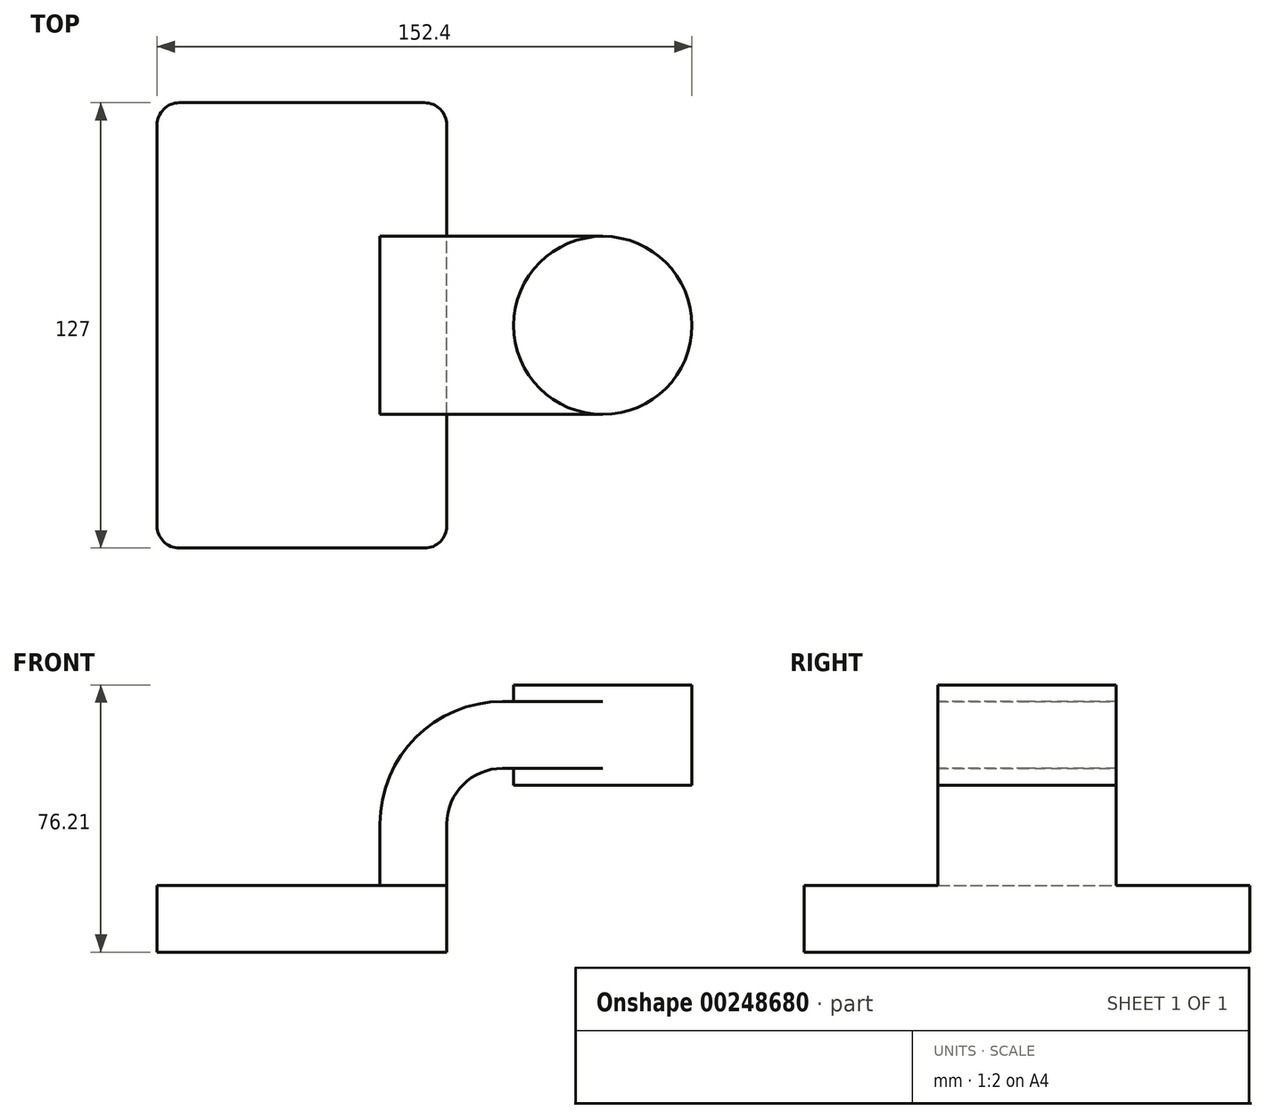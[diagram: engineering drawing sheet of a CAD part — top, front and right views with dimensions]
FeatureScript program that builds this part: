
annotation { "Feature Type Name" : "Feature", "Feature Type Description" : "" }
export const myFeature = defineFeature(function(context is Context, id is Id, definition is map)
    precondition{}
    {
        {
            var Q0;
            Q0=qCreatedBy(makeId("Front.planeOp"),FACE);
            var sketch = newSketch(context, id + "F0", { "sketchPlane" : qUnion([Q0])});
            skLineSegment(sketch, "E0.bottom", {"start": v(-41.28, 9.52) * mm, "end": v(41.27, 9.53) * mm});
            skLineSegment(sketch, "E0.top", {"start": v(-41.28, -9.53) * mm, "end": v(41.28, -9.53) * mm});
            skLineSegment(sketch, "E0.left", {"start": v(-41.28, 9.52) * mm, "end": v(-41.27, -9.53) * mm});
            skLineSegment(sketch, "E0.right", {"start": v(41.28, 9.53) * mm, "end": v(41.28, -9.52) * mm});
            skPoint(sketch, "E0.middle", {"position": v(0, 0) * mm});
            skLineSegment(sketch, "E1.bottom", {"start": v(60.32, 66.68) * mm, "end": v(111.12, 66.68) * mm});
            skLineSegment(sketch, "E1.top", {"start": v(60.33, 38.1) * mm, "end": v(111.12, 38.1) * mm});
            skLineSegment(sketch, "E1.left", {"start": v(60.32, 66.68) * mm, "end": v(60.33, 38.1) * mm});
            skLineSegment(sketch, "E1.right", {"start": v(111.12, 66.68) * mm, "end": v(111.12, 38.1) * mm});
            skPoint(sketch, "E1.middle", {"position": v(85.72, 52.39) * mm});
            skLineSegment(sketch, "E2", {"start": v(41.27, 9.53) * mm, "end": v(41.27, 27) * mm});
            skArc(sketch, "E3", {"start": v(41.27, 27) * mm, "mid": v(45.92, 38.23) * mm, "end": v(57.15, 42.88) * mm});
            skLineSegment(sketch, "E4", {"start": v(57.15, 42.88) * mm, "end": v(85.72, 42.88) * mm});
            skLineSegment(sketch, "E5.0", {"start": v(57.15, 61.93) * mm, "end": v(85.72, 61.93) * mm});
            skArc(sketch, "E5.1", {"start": v(22.22, 27) * mm, "mid": v(32.45, 51.7) * mm, "end": v(57.15, 61.93) * mm});
            skLineSegment(sketch, "E5.2", {"start": v(22.22, 9.53) * mm, "end": v(22.22, 27) * mm});
            skLineSegment(sketch, "E6", {"start": v(85.72, 38.1) * mm, "end": v(85.72, 66.68) * mm});
            skFitSpline(sketch, "E7", {"points": [v(-41.27, 9.52) * mm, v(57.15, 61.93) * mm], "startDerivative": vector(2.24, 52.43) * mm, "endDerivative": vector(126.21, -7.9) * mm});
            skSolve(sketch);
        }
        {
            var Q0;
            Q0=makeQuery(id+"F0.imprint","IMPRINT",FACE,{"disambiguationData":[TD([[makeQuery(id+"F0.imprint","IMPRINT",EDGE,{"derivedFrom":sQuery(id+"F0.wireOp",EDGE,"E0.top")}),1.0]])]});
            extrude(context, id + "F1", {"entities" : qUnion([Q0]), "endBound" : BoundingType.SYMMETRIC, "depth" : 127 * mm});
        }
        {
            var Q0;
            {var subQ1=sQuery(id+"F0.wireOp",EDGE,"E2");Q0=makeQuery(id+"F0.imprint","IMPRINT",FACE,{"disambiguationData":[TD([[makeQuery(id+"F0.imprint","IMPRINT",EDGE,{"derivedFrom":subQ1}),1.0]])]});}
            var Q1;
            {var subQ0=sQuery(id+"F0.wireOp",EDGE,"E5.0");var subQ1=sQuery(id+"F0.wireOp",EDGE,"E1.left");var subQ2=makeQuery(id+"F0.imprint","INTERSECT",VERTEX,{"derivedFrom":[subQ1,subQ0]});Q1=makeQuery(id+"F0.imprint","IMPRINT",FACE,{"disambiguationData":[TD([[makeQuery(id+"F0.imprint","IMPRINT",EDGE,{"disambiguationData":[TD([[subQ2,-1.0]])],"derivedFrom":subQ1}),1.0]])]});}
            extrude(context, id + "F2", {"entities" : qUnion([Q0, Q1]), "operationType" : NewBodyOperationType.ADD, "endBound" : BoundingType.SYMMETRIC, "depth" : 50.8 * mm});
        }
        {
            var Q0;
            Q0=makeQuery(id+"F0.imprint","IMPRINT",FACE,{"disambiguationData":[TD([[makeQuery(id+"F0.imprint","IMPRINT",EDGE,{"derivedFrom":sQuery(id+"F0.wireOp",EDGE,"E5.1")}),1.0]])]});
            extrude(context, id + "F3", {"entities" : qUnion([Q0]), "operationType" : NewBodyOperationType.ADD, "endBound" : BoundingType.SYMMETRIC, "depth" : 25.4 * mm});
        }
        {
            var Q0;
            {var subQ0=sQuery(id+"F0.wireOp",EDGE,"E1.right");Q0=makeQuery(id+"F0.imprint","IMPRINT",FACE,{"disambiguationData":[TD([[makeQuery(id+"F0.imprint","IMPRINT",EDGE,{"derivedFrom":subQ0}),-1.0]])]});}
            var Q1;
            Q1=sQuery(id+"F0.wireOp",EDGE,"E6");
            revolve(context, id + "F4", {"operationType" : NewBodyOperationType.ADD, "entities" : qUnion([Q0]), "axis" : qUnion([Q1]), "revolveType" : RevolveType.FULL});
        }
        {
            var Q0;
            Q0=makeQuery(id+"F1.opExtrude","CAP_EDGE",EDGE,{"disambiguationData":[OSD([sQuery(id+"F0.wireOp",EDGE,"E0.left")])],"isStart":false});
            fillet(context, id + "F5", {"entities" : qUnion([Q0]), "radius" : 6.35 * mm, "tangentPropagation" : true, "allowEdgeOverflow" : false});
        }
        {
            var Q0;
            Q0=makeQuery(id+"F1.opExtrude","CAP_EDGE",EDGE,{"disambiguationData":[OSD([sQuery(id+"F0.wireOp",EDGE,"E0.right")])],"isStart":false});
            fillet(context, id + "F6", {"entities" : qUnion([Q0]), "radius" : 6.35 * mm, "tangentPropagation" : true, "allowEdgeOverflow" : false});
        }
        {
            var Q0;
            Q0=makeQuery(id+"F1.opExtrude","CAP_EDGE",EDGE,{"disambiguationData":[OSD([sQuery(id+"F0.wireOp",EDGE,"E0.right")])],"isStart":true});
            fillet(context, id + "F7", {"entities" : qUnion([Q0]), "radius" : 6.35 * mm, "tangentPropagation" : true, "allowEdgeOverflow" : false});
        }
        {
            var Q0;
            Q0=makeQuery(id+"F1.opExtrude","CAP_EDGE",EDGE,{"disambiguationData":[OSD([sQuery(id+"F0.wireOp",EDGE,"E0.left")])],"isStart":true});
            fillet(context, id + "F8", {"entities" : qUnion([Q0]), "radius" : 6.35 * mm, "tangentPropagation" : true, "allowEdgeOverflow" : false});
        }
    });
